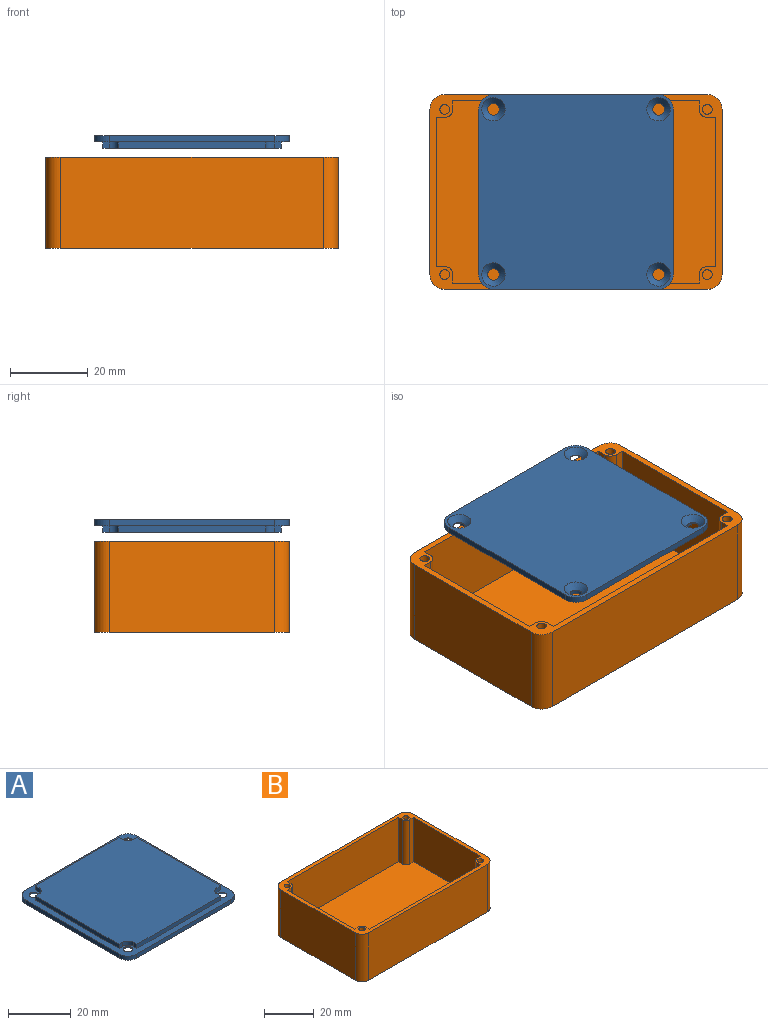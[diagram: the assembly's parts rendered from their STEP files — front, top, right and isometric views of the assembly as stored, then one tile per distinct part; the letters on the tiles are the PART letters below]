
ASSEMBLY  parts=2 mates=1
PART A: 35 faces, bbox 50x50x3.2 mm
  f0: cylinder r=1.5mm len=3mm, axis (0,0,1), area 0.9mm2, adj f20,f31
  f1: cylinder r=1.5mm len=3mm, axis (0,0,1), area 0.9mm2, adj f20,f33
  f2: plane 50x50mm, normal (0,0,-1), area 2374.5mm2, adj f21,f22,f23,f24,f25,f26,f27,f30
  f3: cylinder r=2.3mm len=2.3mm, axis (0,0,-1), area 5.8mm2, adj f4,f18,f19,f20
  f4: plane 1.7x1.6mm, normal (1,0,0), area 2.7mm2, adj f3,f5,f19,f20
  f5: plane 37.8x1.6mm, normal (0,1,0), area 60.5mm2, adj f4,f6,f19,f20
  f6: plane 1.7x1.6mm, normal (-1,0,0), area 2.7mm2, adj f5,f7,f19,f20
  f7: cylinder r=2.3mm len=2.3mm, axis (0,0,-1), area 5.8mm2, adj f6,f8,f19,f20
  f8: plane 1.7x1.6mm, normal (0,1,0), area 2.7mm2, adj f7,f9,f19,f20
  f9: plane 37.8x1.6mm, normal (-1,0,0), area 60.5mm2, adj f8,f10,f19,f20
  f10: plane 1.7x1.6mm, normal (0,-1,0), area 2.7mm2, adj f9,f11,f19,f20
  f11: cylinder r=2.3mm len=2.3mm, axis (0,0,-1), area 5.8mm2, adj f10,f12,f19,f20
  f12: plane 1.7x1.6mm, normal (-1,0,0), area 2.7mm2, adj f11,f13,f19,f20
  f13: plane 37.8x1.6mm, normal (0,-1,0), area 60.5mm2, adj f12,f14,f19,f20
  f14: plane 1.7x1.6mm, normal (1,0,0), area 2.7mm2, adj f13,f15,f19,f20
  f15: cylinder r=2.3mm len=2.3mm, axis (0,0,-1), area 5.8mm2, adj f14,f16,f19,f20
  f16: plane 1.7x1.6mm, normal (0,-1,0), area 2.7mm2, adj f15,f17,f19,f20
  f17: plane 37.8x1.6mm, normal (1,0,0), area 60.5mm2, adj f16,f18,f19,f20
  f18: plane 1.7x1.6mm, normal (0,1,0), area 2.7mm2, adj f3,f17,f19,f20
  f19: plane 45.8x45.8mm, normal (0,0,1), area 2038.2mm2, adj f3,f4,f5,f6,f7,f8,f9,f10
  f20: plane 50x50mm, normal (0,0,1), area 421.1mm2, adj f0,f1,f3,f4,f5,f6,f7,f8
  f21: plane 42.4x1.6mm, normal (0,1,0), area 67.8mm2, adj f2,f20,f22,f30
  f22: cylinder r=3.8mm len=3.8mm, axis (0,0,1), area 9.6mm2, adj f2,f20,f21,f23
  f23: plane 42.4x1.6mm, normal (-1,0,0), area 67.8mm2, adj f2,f20,f22,f24
  f24: cylinder r=3.8mm len=3.8mm, axis (0,0,1), area 9.6mm2, adj f2,f20,f23,f25
  f25: plane 42.4x1.6mm, normal (0,-1,0), area 67.8mm2, adj f2,f20,f24,f26
  f26: cylinder r=3.8mm len=3.8mm, axis (0,0,1), area 9.6mm2, adj f2,f20,f25,f27
  f27: plane 42.4x1.6mm, normal (1,0,0), area 67.8mm2, adj f2,f20,f26,f30
  f28: cylinder r=1.5mm len=3mm, axis (0,0,1), area 0.9mm2, adj f20,f34
  f29: cylinder r=1.5mm len=3mm, axis (0,0,1), area 0.9mm2, adj f20,f32
  f30: cylinder r=3.8mm len=3.8mm, axis (0,0,1), area 9.6mm2, adj f2,f20,f21,f27
  f31: cone r=3mm half-angle=45deg, axis (0,0,-1), area 30mm2, adj f0,f2
  f32: cone r=3mm half-angle=45deg, axis (0,0,-1), area 30mm2, adj f2,f29
  f33: cone r=3mm half-angle=45deg, axis (0,0,-1), area 30mm2, adj f1,f2
  f34: cone r=3mm half-angle=45deg, axis (0,0,-1), area 30mm2, adj f2,f28
PART B: 35 faces, bbox 75x50x23.4 mm
  f0: plane 67.4x23.4mm, normal (0,1,0), area 1577.2mm2, adj f1,f7,f8,f29
  f1: cylinder r=3.8mm len=23.4mm, axis (0,0,1), area 139.7mm2, adj f0,f2,f8,f29
  f2: plane 42.4x23.4mm, normal (-1,0,0), area 992.2mm2, adj f1,f3,f8,f29
  f3: cylinder r=3.8mm len=23.4mm, axis (0,0,1), area 139.7mm2, adj f2,f4,f8,f29
  f4: plane 67.4x23.4mm, normal (0,-1,0), area 1577.2mm2, adj f3,f5,f8,f29
  f5: cylinder r=3.8mm len=23.4mm, axis (0,0,1), area 139.7mm2, adj f4,f6,f8,f29
  f6: plane 42.4x23.4mm, normal (1,0,0), area 992.2mm2, adj f5,f7,f8,f29
  f7: cylinder r=3.8mm len=23.4mm, axis (0,0,1), area 139.7mm2, adj f0,f6,f8,f29
  f8: plane 75x50mm, normal (0,0,-1), area 3737.6mm2, adj f0,f1,f2,f3,f4,f5,f6,f7
  f9: plane 21.8x2.2mm, normal (-1,0,0), area 48mm2, adj f10,f28,f29,f33
  f10: cylinder r=2.05mm len=21.8mm, axis (0,0,-1), area 70.2mm2, adj f9,f11,f29,f33
  f11: plane 21.8x2.2mm, normal (0,-1,0), area 48mm2, adj f10,f12,f29,f33
  f12: plane 38.3x21.8mm, normal (-1,0,0), area 834.9mm2, adj f11,f13,f29,f33
  f13: plane 21.8x2.2mm, normal (0,1,0), area 48mm2, adj f12,f14,f29,f33
  f14: cylinder r=2.05mm len=21.8mm, axis (0,0,-1), area 70.2mm2, adj f13,f15,f29,f33
  f15: plane 21.8x2.2mm, normal (-1,0,0), area 48mm2, adj f14,f16,f29,f33
  f16: plane 63.3x21.8mm, normal (0,1,0), area 1379.9mm2, adj f15,f17,f29,f33
  f17: plane 21.8x2.2mm, normal (1,0,0), area 48mm2, adj f16,f18,f29,f33
  f18: cylinder r=2.05mm len=21.8mm, axis (0,0,-1), area 70.2mm2, adj f17,f19,f29,f33
  f19: plane 21.8x2.2mm, normal (0,1,0), area 48mm2, adj f18,f20,f29,f33
  f20: plane 38.3x21.8mm, normal (1,0,0), area 834.9mm2, adj f19,f21,f29,f33
  f21: plane 21.8x2.2mm, normal (0,-1,0), area 48mm2, adj f20,f22,f29,f33
  f22: cylinder r=2.05mm len=21.8mm, axis (0,0,-1), area 70.2mm2, adj f21,f23,f29,f33
  f23: plane 21.8x2.2mm, normal (1,0,0), area 48mm2, adj f22,f28,f29,f33
  f24: cylinder r=1.25mm len=21.8mm, axis (0,0,-1), area 171.2mm2, adj f29,f34
  f25: cylinder r=1.25mm len=21.8mm, axis (0,0,-1), area 171.2mm2, adj f29,f30
  f26: cylinder r=1.25mm len=21.8mm, axis (0,0,-1), area 171.2mm2, adj f29,f31
  f27: cylinder r=1.25mm len=21.8mm, axis (0,0,-1), area 171.2mm2, adj f29,f32
  f28: plane 63.3x21.8mm, normal (0,-1,0), area 1379.9mm2, adj f9,f23,f29,f33
  f29: plane 75x50mm, normal (0,0,1), area 426.4mm2, adj f0,f1,f2,f3,f4,f5,f6,f7
  f30: plane 2.5x2.5mm, normal (0,0,1), area 4.9mm2, adj f25
  f31: plane 2.5x2.5mm, normal (0,0,1), area 4.9mm2, adj f26
  f32: plane 2.5x2.5mm, normal (0,0,1), area 4.9mm2, adj f27
  f33: plane 71.8x46.8mm, normal (0,0,1), area 3291.6mm2, adj f9,f10,f11,f12,f13,f14,f15,f16
  f34: plane 2.5x2.5mm, normal (0,0,1), area 4.9mm2, adj f24
PLACE A rot(axis=(1,0,0),180deg) t=(6.85,4.34,9.48)mm
PLACE B t=(6.85,4.34,-16.22)mm
MATE pin_slot A.f0 <-> B.f3  axis (0,0,1) through (-14.35,-16.86,9.58)mm
